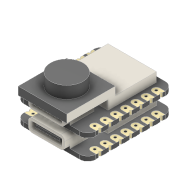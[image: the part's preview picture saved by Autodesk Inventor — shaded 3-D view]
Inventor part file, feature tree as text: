
AUTODESK INVENTOR PART (.ipt)
format: ipt  version: 2022 (Build 260153000, 153)  size: 451,584 bytes
history: native  units: mm
features: extrude x2, sketch x2, projected_geometry x2, pattern_linear x1
ambient origin geometry x8: Origin, YZ Plane, XZ Plane, XY Plane, X Axis, Y Axis, Z Axis, Center Point
bodies: Volumenkörper1 (feature_tree), Body1 (feature_tree)
feature tree (7):
  extrude  "Extrusion1"  Depth=5.0mm TaperAngle=0.0deg
  extrude  "Extrusion2"  Depth=12.0mm
  pattern_linear  "Rechteckige Anordnung1"  Spacing1=2.0mm  [1 undecoded]
  sketch  "Skizze1"  dims[d0=8.0mm d1=5.0mm d2=0.0mm]
  projected_geometry  "Projizierte Kontur1"
  sketch  "Skizze2"  dims[d3=12.0mm d4=12.0mm d5=2.0mm d6=0.0mm d7=20.0mm d9=5.0mm]
  projected_geometry  "Projizierte Kontur2"
note: 1 required parameter value undecoded (feature->parameter linkage not recoverable at this tier; creation-order binding heuristic only, values carry confidence <= 0.55)
